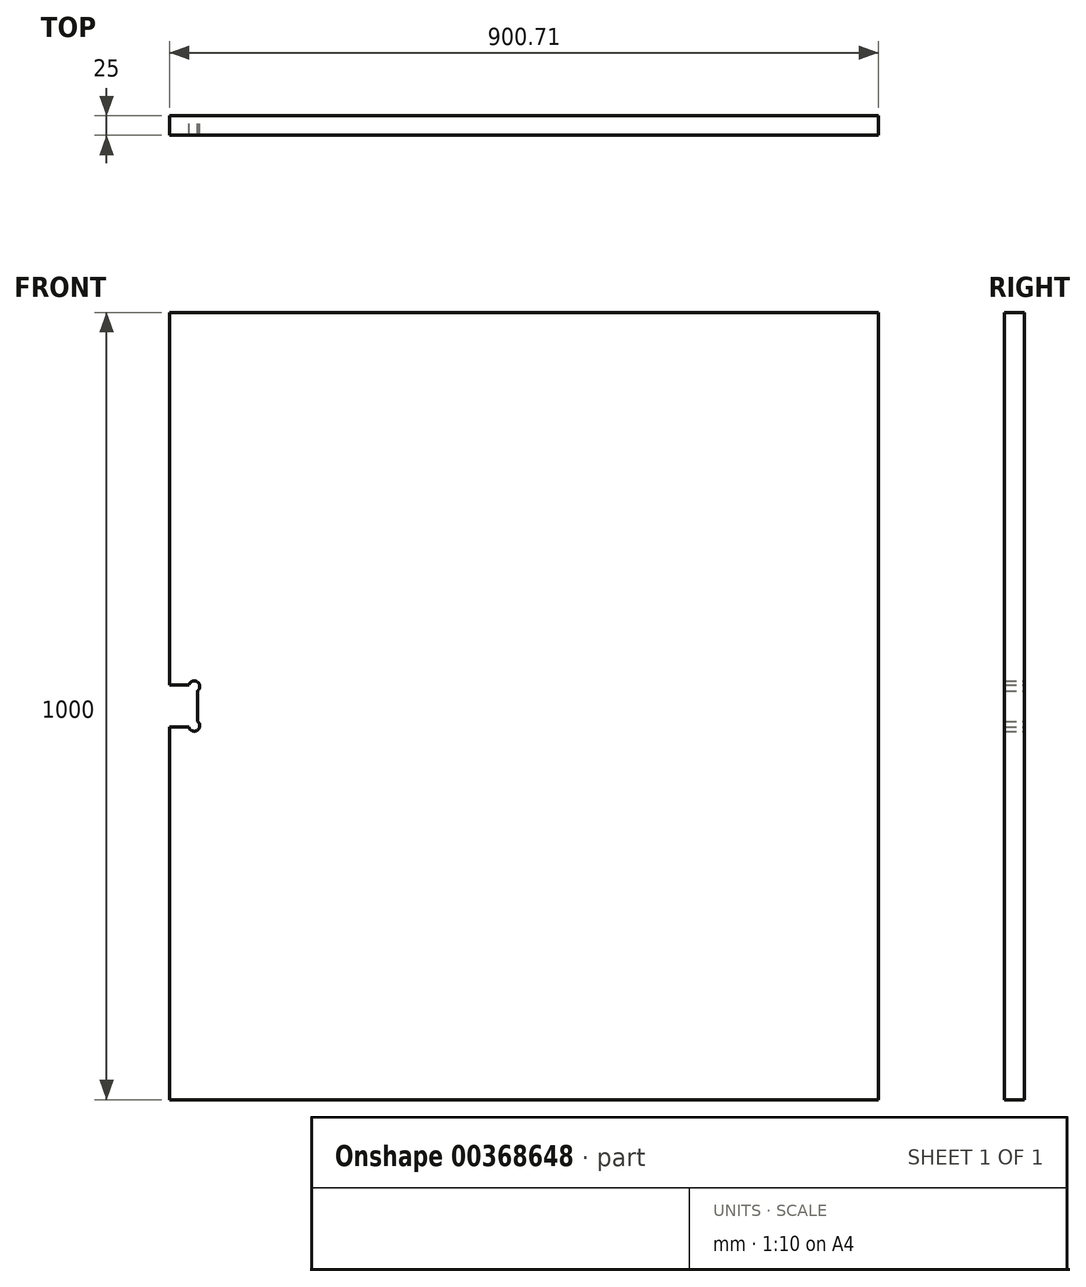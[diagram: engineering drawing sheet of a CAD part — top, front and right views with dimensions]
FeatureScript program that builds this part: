
annotation { "Feature Type Name" : "Feature", "Feature Type Description" : "" }
export const myFeature = defineFeature(function(context is Context, id is Id, definition is map)
    precondition{}
    {
        {
            var Q0;
            Q0=qCreatedBy(makeId("Front.planeOp"),FACE);
            var sketch = newSketch(context, id + "F0", { "sketchPlane" : qUnion([Q0])});
            skLineSegment(sketch, "E0", {"start": v(0, 500) * mm, "end": v(0, 26.5) * mm});
            skLineSegment(sketch, "E1", {"start": v(0, 26.5) * mm, "end": v(24.66, 26.5) * mm});
            skArc(sketch, "E2", {"start": v(35.5, 19.26) * mm, "mid": v(35.4, 30.82) * mm, "end": v(24.66, 26.5) * mm});
            skLineSegment(sketch, "E3", {"start": v(35.5, 19.26) * mm, "end": v(35.5, -19.26) * mm});
            skArc(sketch, "E4", {"start": v(24.66, -26.5) * mm, "mid": v(35.4, -30.82) * mm, "end": v(35.5, -19.26) * mm});
            skLineSegment(sketch, "E5", {"start": v(24.66, -26.5) * mm, "end": v(0, -26.5) * mm});
            skLineSegment(sketch, "E6", {"start": v(0, -26.5) * mm, "end": v(0, -500) * mm});
            skLineSegment(sketch, "E7", {"start": v(0, 500) * mm, "end": v(900.71, 500) * mm});
            skLineSegment(sketch, "E8", {"start": v(900.71, 500) * mm, "end": v(900.71, -500) * mm});
            skLineSegment(sketch, "E9", {"start": v(900.71, -500) * mm, "end": v(0, -500) * mm});
            skSolve(sketch);
        }
        {
            var Q0;
            Q0 = qSketchRegion(id + "F0", true);
            extrude(context, id + "F1", {"entities" : qUnion([Q0]), "depth" : 25 * mm});
        }
    });
